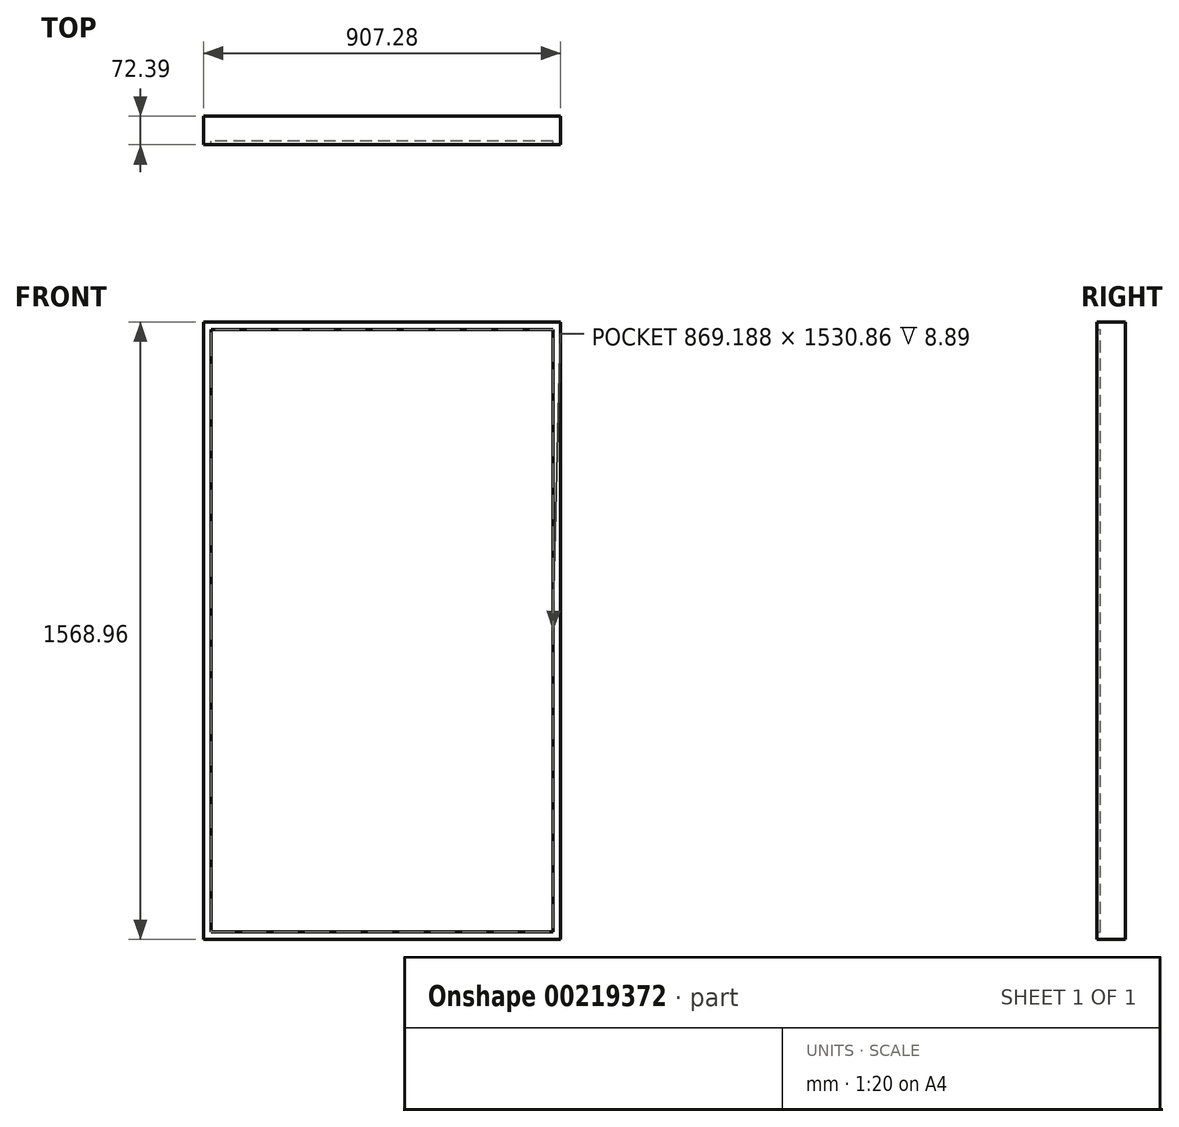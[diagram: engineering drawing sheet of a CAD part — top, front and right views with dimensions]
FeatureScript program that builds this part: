
annotation { "Feature Type Name" : "Feature", "Feature Type Description" : "" }
export const myFeature = defineFeature(function(context is Context, id is Id, definition is map)
    precondition{}
    {
        {
            var Q0;
            Q0=qCreatedBy(makeId("Front.planeOp"),FACE);
            var sketch = newSketch(context, id + "F0", { "sketchPlane" : qUnion([Q0])});
            skLineSegment(sketch, "E0.bottom", {"start": v(453.64, -784.48) * mm, "end": v(-453.64, -784.48) * mm});
            skLineSegment(sketch, "E0.top", {"start": v(453.64, 784.48) * mm, "end": v(-453.64, 784.48) * mm});
            skLineSegment(sketch, "E0.left", {"start": v(453.64, -784.48) * mm, "end": v(453.64, 784.48) * mm});
            skLineSegment(sketch, "E0.right", {"start": v(-453.64, -784.48) * mm, "end": v(-453.64, 784.48) * mm});
            skPoint(sketch, "E0.middle", {"position": v(0, 0) * mm});
            skLineSegment(sketch, "E1.bottom", {"start": v(434.6, -765.43) * mm, "end": v(-434.6, -765.43) * mm});
            skLineSegment(sketch, "E1.top", {"start": v(434.6, 765.43) * mm, "end": v(-434.6, 765.43) * mm});
            skLineSegment(sketch, "E1.left", {"start": v(434.6, -765.43) * mm, "end": v(434.6, 765.43) * mm});
            skLineSegment(sketch, "E1.right", {"start": v(-434.6, -765.43) * mm, "end": v(-434.6, 765.43) * mm});
            skSolve(sketch);
        }
        {
            var Q0;
            Q0=makeQuery(id+"F0.imprint","IMPRINT",FACE,{"disambiguationData":[TD([[makeQuery(id+"F0.imprint","IMPRINT",EDGE,{"derivedFrom":sQuery(id+"F0.wireOp",EDGE,"E1.bottom")}),-1.0]])]});
            extrude(context, id + "F1", {"entities" : qUnion([Q0]), "depth" : 63.5 * mm});
        }
        {
            var Q0;
            Q0=makeQuery(id+"F0.imprint","IMPRINT",FACE,{"disambiguationData":[TD([[makeQuery(id+"F0.imprint","IMPRINT",EDGE,{"derivedFrom":sQuery(id+"F0.wireOp",EDGE,"E0.bottom")}),-1.0]])]});
            extrude(context, id + "F2", {"entities" : qUnion([Q0]), "operationType" : NewBodyOperationType.ADD, "depth" : 72.39 * mm});
        }
    });
